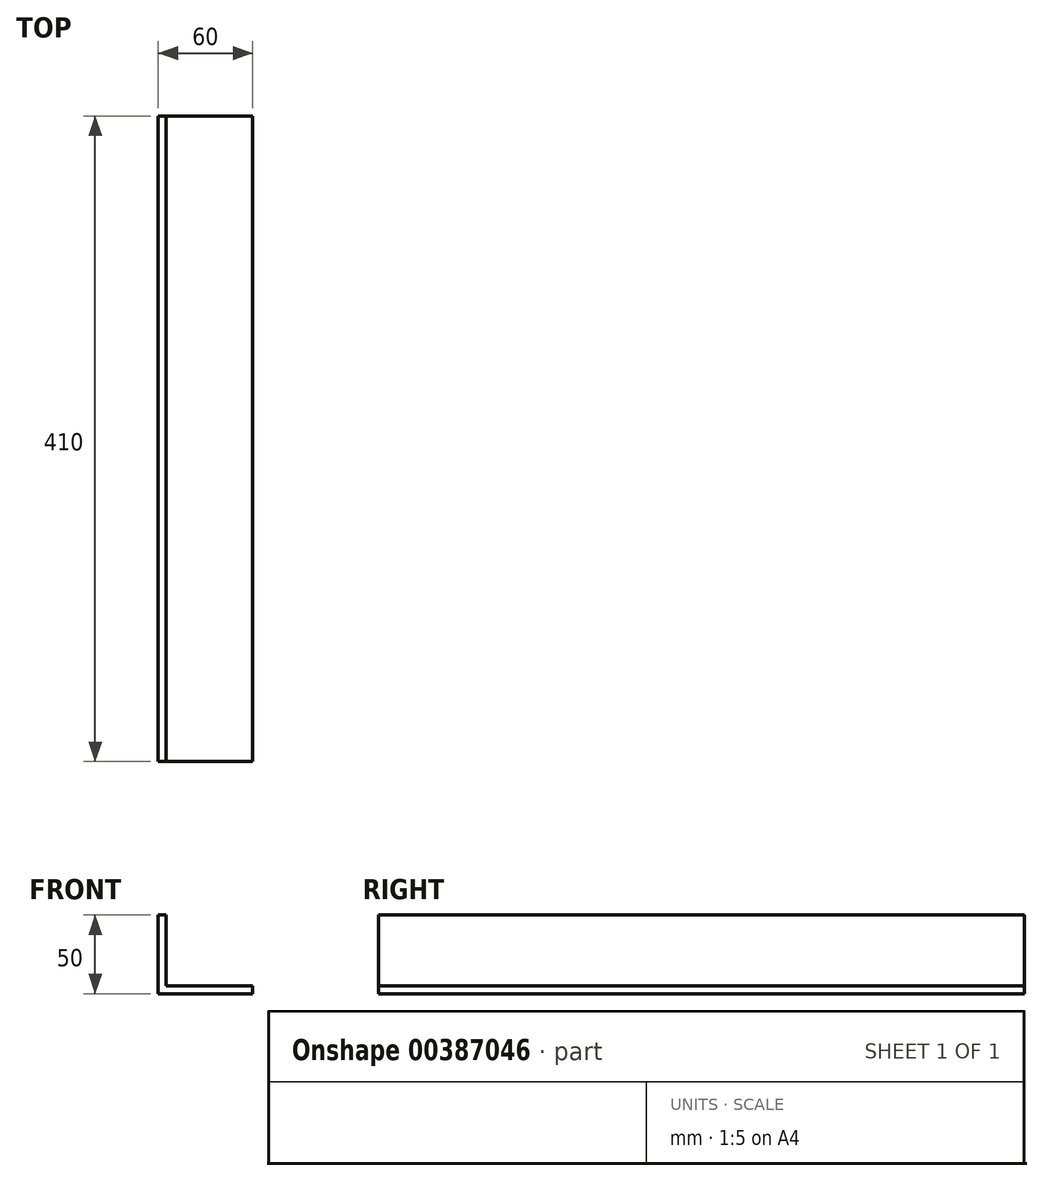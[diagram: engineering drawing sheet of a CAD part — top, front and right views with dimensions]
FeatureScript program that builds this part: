
annotation { "Feature Type Name" : "Feature", "Feature Type Description" : "" }
export const myFeature = defineFeature(function(context is Context, id is Id, definition is map)
    precondition{}
    {
        {
            var Q0;
            Q0=qCreatedBy(makeId("Front.planeOp"),FACE);
            var sketch = newSketch(context, id + "F0", { "sketchPlane" : qUnion([Q0])});
            skLineSegment(sketch, "E0", {"start": v(0, 0) * mm, "end": v(0, 50) * mm});
            skLineSegment(sketch, "E1", {"start": v(0, 50) * mm, "end": v(5, 50) * mm});
            skLineSegment(sketch, "E2", {"start": v(5, 50) * mm, "end": v(5, 5) * mm});
            skLineSegment(sketch, "E3", {"start": v(5, 5) * mm, "end": v(60, 5) * mm});
            skLineSegment(sketch, "E4", {"start": v(60, 5) * mm, "end": v(60, 0) * mm});
            skLineSegment(sketch, "E5", {"start": v(60, 0) * mm, "end": v(0, 0) * mm});
            skSolve(sketch);
        }
        {
            var Q0;
            Q0 = qSketchRegion(id + "F0", true);
            extrude(context, id + "F1", {"entities" : qUnion([Q0]), "depth" : 410 * mm});
        }
    });
